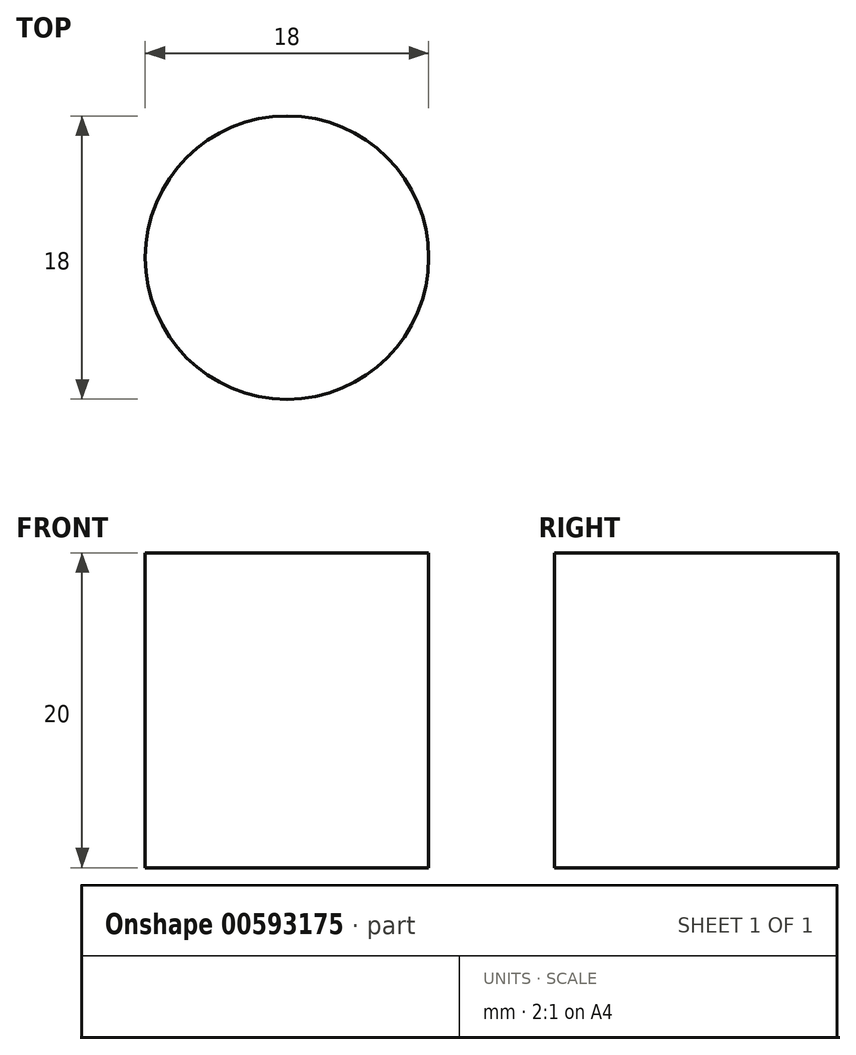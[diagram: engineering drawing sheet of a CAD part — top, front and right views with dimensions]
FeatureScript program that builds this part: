
annotation { "Feature Type Name" : "Feature", "Feature Type Description" : "" }
export const myFeature = defineFeature(function(context is Context, id is Id, definition is map)
    precondition{}
    {
        {
            var Q0;
            Q0=qCreatedBy(makeId("Top.planeOp"),FACE);
            var sketch = newSketch(context, id + "F0", { "sketchPlane" : qUnion([Q0])});
            skCircle(sketch, "E0", {"center": v(-5.99, 11.5) * mm, "radius": 9 * mm});
            skSolve(sketch);
        }
        {
            var Q0;
            Q0=makeQuery(id+"F0.imprint","IMPRINT",FACE,{"disambiguationData":[TD([[makeQuery(id+"F0.imprint","IMPRINT",EDGE,{"derivedFrom":sQuery(id+"F0.wireOp",EDGE,"E0")}),1.0]])]});
            extrude(context, id + "F1", {"entities" : qUnion([Q0]), "depth" : 20 * mm, "offsetDistance" : 25.4 * mm});
        }
    });
